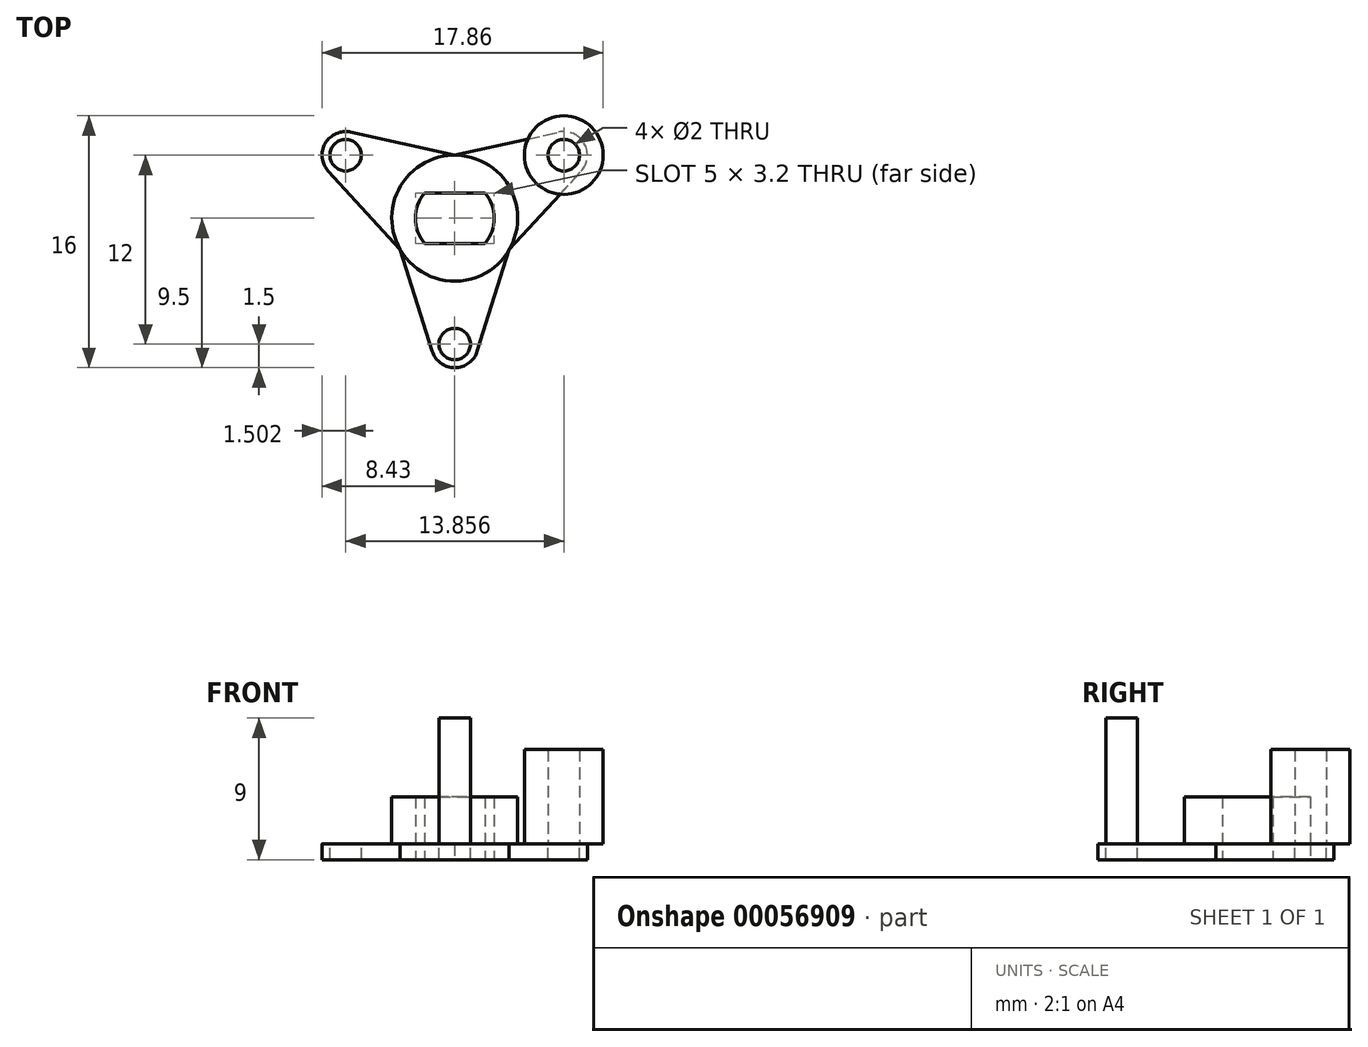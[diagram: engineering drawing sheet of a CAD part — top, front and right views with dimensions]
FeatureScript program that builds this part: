
annotation { "Feature Type Name" : "Feature", "Feature Type Description" : "" }
export const myFeature = defineFeature(function(context is Context, id is Id, definition is map)
    precondition{}
    {
        {
            var Q0;
            Q0=qCreatedBy(makeId("Top.planeOp"),FACE);
            var sketch = newSketch(context, id + "F0", { "sketchPlane" : qUnion([Q0])});
            skCircle(sketch, "E0.cCircle", {"center": v(0, 0) * mm, "radius": 4 * mm, "construction": true});
            skLineSegment(sketch, "E0.0", {"start": v(-6.93, 4) * mm, "end": v(6.93, 4) * mm});
            skLineSegment(sketch, "E0.1", {"start": v(6.93, 4) * mm, "end": v(0, -8) * mm});
            skLineSegment(sketch, "E0.2", {"start": v(0, -8) * mm, "end": v(-6.93, 4) * mm});
            skPoint(sketch, "E0.0.midPoint", {"position": v(0, 4) * mm});
            skCircle(sketch, "E1", {"center": v(-6.93, 4) * mm, "radius": 2.5 * mm, "construction": true});
            skCircle(sketch, "E2", {"center": v(6.93, 4) * mm, "radius": 2.5 * mm, "construction": true});
            skCircle(sketch, "E3", {"center": v(0, -8) * mm, "radius": 2.5 * mm, "construction": true});
            skCircle(sketch, "E4", {"center": v(0, 0) * mm, "radius": 10.5 * mm, "construction": true});
            skArc(sketch, "E5", {"start": v(-5.43, 4) * mm, "mid": v(-8.23, 4.75) * mm, "end": v(-6.18, 2.7) * mm});
            skArc(sketch, "E6", {"start": v(6.18, 2.7) * mm, "mid": v(8.23, 4.75) * mm, "end": v(5.43, 4) * mm});
            skArc(sketch, "E7", {"start": v(-0.75, -6.7) * mm, "mid": v(0, -9.5) * mm, "end": v(0.75, -6.7) * mm});
            skLineSegment(sketch, "E8", {"start": v(-3.46, -2) * mm, "end": v(-8.03, 2.99) * mm});
            skLineSegment(sketch, "E9", {"start": v(0, 4) * mm, "end": v(-6.6, 5.46) * mm});
            skLineSegment(sketch, "E10.1.0", {"start": v(-3.46, -2) * mm, "end": v(-1.43, -8.45) * mm});
            skLineSegment(sketch, "E10.1.1", {"start": v(3.46, -2) * mm, "end": v(1.43, -8.45) * mm});
            skLineSegment(sketch, "E10.2.0", {"start": v(3.46, -2) * mm, "end": v(8.03, 2.99) * mm});
            skLineSegment(sketch, "E10.2.1", {"start": v(0, 4) * mm, "end": v(6.6, 5.46) * mm});
            skSolve(sketch);
        }
        {
            var Q0;
            Q0=qSketchRegion(id+"F0",true);
            extrude(context, id + "F1", {"entities" : qUnion([Q0]), "depth" : 1 * mm});
        }
        {
            var Q0;
            Q0=makeQuery(id+"F1.opExtrude","CAP_FACE",FACE,{"disambiguationData":[OSD([sQuery(id+"F0.wireOp",EDGE,"E5"),sQuery(id+"F0.wireOp",EDGE,"E6"),sQuery(id+"F0.wireOp",EDGE,"E7"),sQuery(id+"F0.wireOp",EDGE,"E8"),sQuery(id+"F0.wireOp",EDGE,"E9"),sQuery(id+"F0.wireOp",EDGE,"E10.1.0"),sQuery(id+"F0.wireOp",EDGE,"E10.1.1"),sQuery(id+"F0.wireOp",EDGE,"E10.2.0"),sQuery(id+"F0.wireOp",EDGE,"E10.2.1")])],"isStart":true});
            var sketch = newSketch(context, id + "F2", { "sketchPlane" : qUnion([Q0])});
            skArc(sketch, "E11", {"start": v(-1.92, 1.6) * mm, "mid": v(-2.5, 0) * mm, "end": v(-1.92, -1.6) * mm});
            skLineSegment(sketch, "E12.rect.bottom", {"start": v(-1.92, 1.6) * mm, "end": v(1.92, 1.6) * mm});
            skLineSegment(sketch, "E12.rect.top", {"start": v(-1.92, -1.6) * mm, "end": v(1.92, -1.6) * mm});
            skLineSegment(sketch, "E12.rect.left", {"start": v(-1.92, 1.6) * mm, "end": v(-1.92, -1.6) * mm});
            skLineSegment(sketch, "E12.rect.right", {"start": v(1.92, 1.6) * mm, "end": v(1.92, -1.6) * mm});
            skArc(sketch, "E13.trimOffspring", {"start": v(1.92, -1.6) * mm, "mid": v(2.5, 0) * mm, "end": v(1.92, 1.6) * mm});
            skSolve(sketch);
        }
        {
            var Q0;
            Q0=qSketchRegion(id+"F2",true);
            extrude(context, id + "F3", {"entities" : qUnion([Q0]), "operationType" : NewBodyOperationType.REMOVE, "endBound" : BoundingType.THROUGH_ALL, "oppositeDirection" : true, "depth" : 25 * mm});
        }
        {
            var Q0;
            Q0=makeQuery(id+"F1.opExtrude","CAP_FACE",FACE,{"disambiguationData":[OSD([sQuery(id+"F0.wireOp",EDGE,"E5"),sQuery(id+"F0.wireOp",EDGE,"E6"),sQuery(id+"F0.wireOp",EDGE,"E7"),sQuery(id+"F0.wireOp",EDGE,"E8"),sQuery(id+"F0.wireOp",EDGE,"E9"),sQuery(id+"F0.wireOp",EDGE,"E10.1.0"),sQuery(id+"F0.wireOp",EDGE,"E10.1.1"),sQuery(id+"F0.wireOp",EDGE,"E10.2.0"),sQuery(id+"F0.wireOp",EDGE,"E10.2.1")])],"isStart":false});
            var sketch = newSketch(context, id + "F4", { "sketchPlane" : qUnion([Q0])});
            skCircle(sketch, "E14", {"center": v(0, 0) * mm, "radius": 4 * mm});
            skLineSegment(sketch, "E15.0", {"start": v(1.92, 1.6) * mm, "end": v(-1.92, 1.6) * mm});
            skArc(sketch, "E15.1", {"start": v(-1.92, 1.6) * mm, "mid": v(-2.5, 0) * mm, "end": v(-1.92, -1.6) * mm});
            skLineSegment(sketch, "E15.2", {"start": v(1.92, -1.6) * mm, "end": v(-1.92, -1.6) * mm});
            skArc(sketch, "E15.3", {"start": v(1.92, -1.6) * mm, "mid": v(2.5, 0) * mm, "end": v(1.92, 1.6) * mm});
            skSolve(sketch);
        }
        {
            var Q0;
            Q0=qSketchRegion(id+"F4",true);
            extrude(context, id + "F5", {"entities" : qUnion([Q0]), "operationType" : NewBodyOperationType.ADD, "depth" : 3 * mm});
        }
        {
            var Q0;
            {var subQ0=sQuery(id+"F0.wireOp",EDGE,"E5");var subQ1=sQuery(id+"F0.wireOp",EDGE,"E8");var subQ2=sQuery(id+"F0.wireOp",EDGE,"E9");var subQ3=sQuery(id+"F0.wireOp",EDGE,"E10.1.0");var subQ4=sQuery(id+"F0.wireOp",EDGE,"E10.2.1");var subQ5=makeQuery(id+"F1.opExtrude","CAP_FACE",FACE,{"disambiguationData":[OSD([subQ0,sQuery(id+"F0.wireOp",EDGE,"E6"),sQuery(id+"F0.wireOp",EDGE,"E7"),subQ1,subQ2,subQ3,sQuery(id+"F0.wireOp",EDGE,"E10.1.1"),sQuery(id+"F0.wireOp",EDGE,"E10.2.0"),subQ4])],"isStart":false});Q0=makeQuery(id+"F5.boolean.opBoolean","SPLIT",FACE,{"disambiguationData":[TD([makeQuery(id+"F1.opExtrude","SWEPT_FACE",FACE,{"disambiguationData":[OSD([subQ0])]})])],"derivedFrom":subQ5});}
            var sketch = newSketch(context, id + "F6", { "sketchPlane" : qUnion([Q0])});
            skCircle(sketch, "E16", {"center": v(-6.93, 4) * mm, "radius": 1 * mm});
            skCircle(sketch, "E17.1.0", {"center": v(0, -8) * mm, "radius": 1 * mm});
            skCircle(sketch, "E17.2.0", {"center": v(6.93, 4) * mm, "radius": 1 * mm});
            skPoint(sketch, "E17.center", {"position": v(0, 0) * mm});
            skSolve(sketch);
        }
        {
            var Q0;
            Q0=qSketchRegion(id+"F6",true);
            extrude(context, id + "F7", {"entities" : qUnion([Q0]), "operationType" : NewBodyOperationType.REMOVE, "endBound" : BoundingType.THROUGH_ALL, "oppositeDirection" : true, "depth" : 25 * mm});
        }
        {
            var Q0;
            {var subQ0=sQuery(id+"F0.wireOp",EDGE,"E7");var subQ1=sQuery(id+"F0.wireOp",EDGE,"E8");var subQ2=sQuery(id+"F0.wireOp",EDGE,"E10.1.0");var subQ3=sQuery(id+"F0.wireOp",EDGE,"E10.1.1");var subQ4=sQuery(id+"F0.wireOp",EDGE,"E10.2.0");var subQ5=makeQuery(id+"F1.opExtrude","CAP_FACE",FACE,{"disambiguationData":[OSD([sQuery(id+"F0.wireOp",EDGE,"E5"),sQuery(id+"F0.wireOp",EDGE,"E6"),subQ0,subQ1,sQuery(id+"F0.wireOp",EDGE,"E9"),subQ2,subQ3,subQ4,sQuery(id+"F0.wireOp",EDGE,"E10.2.1")])],"isStart":false});Q0=makeQuery(id+"F5.boolean.opBoolean","SPLIT",FACE,{"disambiguationData":[TD([makeQuery(id+"F1.opExtrude","SWEPT_FACE",FACE,{"disambiguationData":[OSD([subQ0])]})])],"derivedFrom":subQ5});}
            var sketch = newSketch(context, id + "F8", { "sketchPlane" : qUnion([Q0])});
            skCircle(sketch, "E18.0", {"center": v(0, -8) * mm, "radius": 1 * mm});
            skSolve(sketch);
        }
        {
            var Q0;
            Q0=qSketchRegion(id+"F8",true);
            extrude(context, id + "F9", {"entities" : qUnion([Q0]), "depth" : 8 * mm});
        }
        {
            var Q0;
            {var subQ0=sQuery(id+"F0.wireOp",EDGE,"E6");var subQ1=sQuery(id+"F0.wireOp",EDGE,"E9");var subQ2=sQuery(id+"F0.wireOp",EDGE,"E10.1.1");var subQ3=sQuery(id+"F0.wireOp",EDGE,"E10.2.0");var subQ4=sQuery(id+"F0.wireOp",EDGE,"E10.2.1");var subQ5=makeQuery(id+"F1.opExtrude","CAP_FACE",FACE,{"disambiguationData":[OSD([sQuery(id+"F0.wireOp",EDGE,"E5"),subQ0,sQuery(id+"F0.wireOp",EDGE,"E7"),sQuery(id+"F0.wireOp",EDGE,"E8"),subQ1,sQuery(id+"F0.wireOp",EDGE,"E10.1.0"),subQ2,subQ3,subQ4])],"isStart":false});Q0=makeQuery(id+"F5.boolean.opBoolean","SPLIT",FACE,{"disambiguationData":[TD([makeQuery(id+"F1.opExtrude","SWEPT_FACE",FACE,{"disambiguationData":[OSD([subQ0])]})])],"derivedFrom":subQ5});}
            var sketch = newSketch(context, id + "F10", { "sketchPlane" : qUnion([Q0])});
            skCircle(sketch, "E19.0", {"center": v(6.93, 4) * mm, "radius": 1 * mm});
            skCircle(sketch, "E20", {"center": v(6.93, 4) * mm, "radius": 2.5 * mm});
            skSolve(sketch);
        }
        {
            var Q0;
            Q0=qSketchRegion(id+"F10",true);
            extrude(context, id + "F11", {"entities" : qUnion([Q0]), "depth" : 6 * mm});
        }
    });
